# Revit family: МФ_Eng
name_source: partatom
category: Mechanical Equipment
units: mm (PartAtom-declared; Revit-internal decimal feet)

## family parameters
Always vertical = Yes
Classification = None
Cut with Voids When Loaded = No
Part Type = Normal
Room Calculation Point = No
Round Connector Dimension = Use Diameter
Shared = No
Work Plane-Based = No

## types (3) — shared parameters
00_20_Manufacturer = Vents
00_20_Name = Axial fan
Amperage = 0 A
Casing Material = Plastic, opaque, white
Frequency = 50 Hz
Load Classification = HVAC
Maintenance zone material = <By Category>
Manufacturer = Vents
Number of Fase = 1
URL = https://ventilation-system.com
Voltage = 230 V
zero-valued in all types: Default Elevation

## per-type parameters (varying)
| type | B | D | Diameter | Dy | H | Height | L | L1 | L2 | Length | Maximum Air Flow | Panel | Power | Sound pressure level at 3 m distance | Weight | Width |
| 150 MF | 205 mm  [stored 0.672572 ft] | 150 mm  [stored 0.492126 ft] | 150 mm  [stored 0.492126 ft] | 145 mm  [stored 0.475722 ft] | 205 mm  [stored 0.672572 ft] | 205 mm  [stored 0.672572 ft] | 112 mm  [stored 0.367454 ft] | 23 mm  [stored 0.0754593 ft] | 89 mm  [stored 0.291995 ft] | 112 mm  [stored 0.367454 ft] | 255.0 m³/h | Panel : 150 | 28 W | 35 dBA | 0.97 kg | 112 mm  [stored 0.367454 ft] |
| 100 MF | 150 mm  [stored 0.492126 ft] | 100 mm  [stored 0.328084 ft] | 100 mm  [stored 0.328084 ft] | 95 mm  [stored 0.31168 ft] | 150 mm  [stored 0.492126 ft] | 150 mm  [stored 0.492126 ft] | 79 mm | 19 mm  [stored 0.062336 ft] | 60 mm  [stored 0.19685 ft] | 79 mm | 90.0 m³/h | Panel : 100 | 8 W | 29 dBA | 0.45 kg | 79 mm |
| 125 MF | 180 mm  [stored 0.590551 ft] | 125 mm  [stored 0.410105 ft] | 125 mm  [stored 0.410105 ft] | 120 mm  [stored 0.393701 ft] | 180 mm  [stored 0.590551 ft] | 180 mm  [stored 0.590551 ft] | 85 mm  [stored 0.278871 ft] | 21 mm  [stored 0.0688976 ft] | 64 mm  [stored 0.209974 ft] | 85 mm  [stored 0.278871 ft] | 160.0 m³/h | Panel : 125 | 18 W | 34 dBA | 0.80 kg | 85 mm  [stored 0.278871 ft] |

note: column(s) folded — value = type name in every type: 00_20_Type

note: [stored X ft] marks values corroborated as IEEE doubles in the binary element streams (Revit-internal decimal feet)
